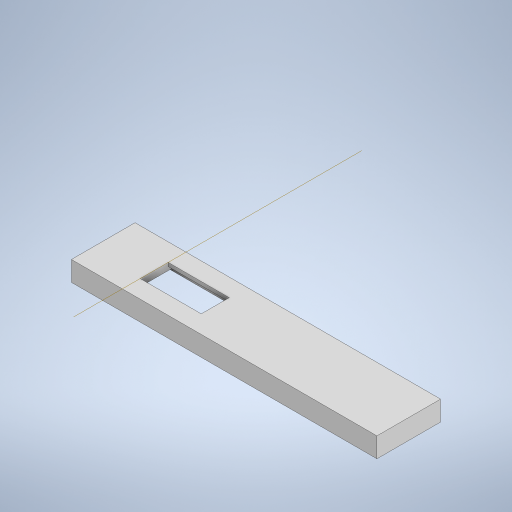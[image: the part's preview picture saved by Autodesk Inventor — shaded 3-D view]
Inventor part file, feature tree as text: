
AUTODESK INVENTOR PART (.ipt)
format: ipt  version: 2023 (Build 270158000, 158)  size: 430,080 bytes
history: native  units: in
note: dims shown in document units (in); Inventor stores cm internally (conversion verified against a paired STEP export)
features: extrude x8, sketch x8, plane x1
ambient origin geometry x8: Origin, YZ Plane, XZ Plane, XY Plane, X Axis, Y Axis, Z Axis, Center Point
bodies: Solid1 (feature_tree)
feature tree (17):
  extrude  "Extrusion1"  Depth=1.25in
  extrude  "Extrusion2"  Depth=0.55in
  extrude  "Extrusion3"  Depth=0.07in TaperAngle=0.0deg
  extrude  "Extrusion4"  TaperAngle=0.0deg  [1 undecoded]
  extrude  "Extrusion5"  Depth=0.0625in
  extrude  "Extrusion6"  Depth=0.25in
  plane  "Work Plane1"
  extrude  "Extrusion7"  Depth=0.1in
  extrude  "Extrusion8"  Depth=1.0in
  sketch  "Sketch1"  dims[d0=6.0in d1=1.25in]
  sketch  "Sketch2"  dims[d2=1.2in d3=0.55in]
  sketch  "Sketch3"  dims[d4=1.0in d5=0.07in d6=0.0in]
  sketch  "Sketch4"  dims[d7=1.2in d8=0.0in]
  sketch  "Sketch5"  dims[d9=0.07in d10=0.0in d11=0.0625in]
  sketch  "Sketch6"  dims[d12=0.25in d13=0.0in d14=0.25in]
  sketch  "Sketch7"  dims[d15=0.1in d16=0.1in]
  sketch  "Sketch8"  dims[d17=0.1in d18=0.1in d19=0.1in d20=0.1in d21=1.0in d22=0.1in d23=0.1in d24=0.1in d25=0.1in d26=0.1in d27=0.1in d28=0.1in d29=0.1in d30=0.1in d31=0.1in d32=0.1in d33=0.1in d34=1.0in d35=1.0in d36=1.0in d37=1.25in d38=0.0in d39=0.1in d40=0.1in d41=0.1in d42=0.1in d43=0.1in d44=0.1in d45=1.0in d46=1.0in d47=0.1in d48=0.1in d49=1.0in d50=0.1in d51=0.1in d52=1.0in d53=1.25in d54=0.0in d55=0.125in d56=0.0in d57=45.0deg d58=0.0in d59=5.0in d60=0.125in d61=0.0in d62=1.0in d63=0.0in]
note: 1 required parameter value undecoded (feature->parameter linkage not recoverable at this tier; creation-order binding heuristic only, values carry confidence <= 0.55)
